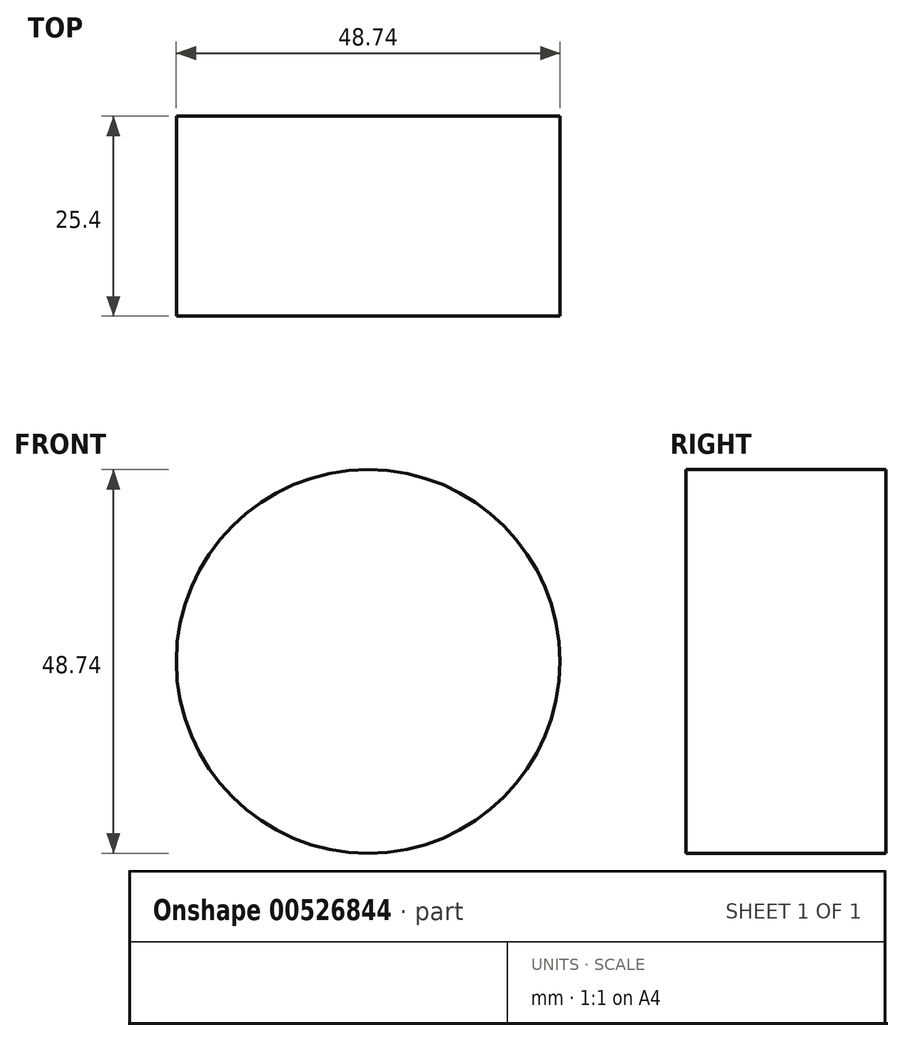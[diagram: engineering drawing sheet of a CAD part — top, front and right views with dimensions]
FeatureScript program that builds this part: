
annotation { "Feature Type Name" : "Feature", "Feature Type Description" : "" }
export const myFeature = defineFeature(function(context is Context, id is Id, definition is map)
    precondition{}
    {
        {
            var Q0;
            Q0=qCreatedBy(makeId("Front.planeOp"),FACE);
            var sketch = newSketch(context, id + "F0", { "sketchPlane" : qUnion([Q0])});
            skCircle(sketch, "E0", {"center": v(0, 43.25) * mm, "radius": 24.37 * mm});
            skCircle(sketch, "E1", {"center": v(0, 43.25) * mm, "radius": 6.96 * mm});
            skSolve(sketch);
        }
        {
            var Q0;
            Q0=sQuery(id+"F0.wireOp",EDGE,"E0");
            extrude(context, id + "F1", {"bodyType" : ToolBodyType.SURFACE, "surfaceEntities" : qUnion([Q0]), "depth" : 25.4 * mm, "offsetDistance" : 25.4 * mm});
        }
    });
